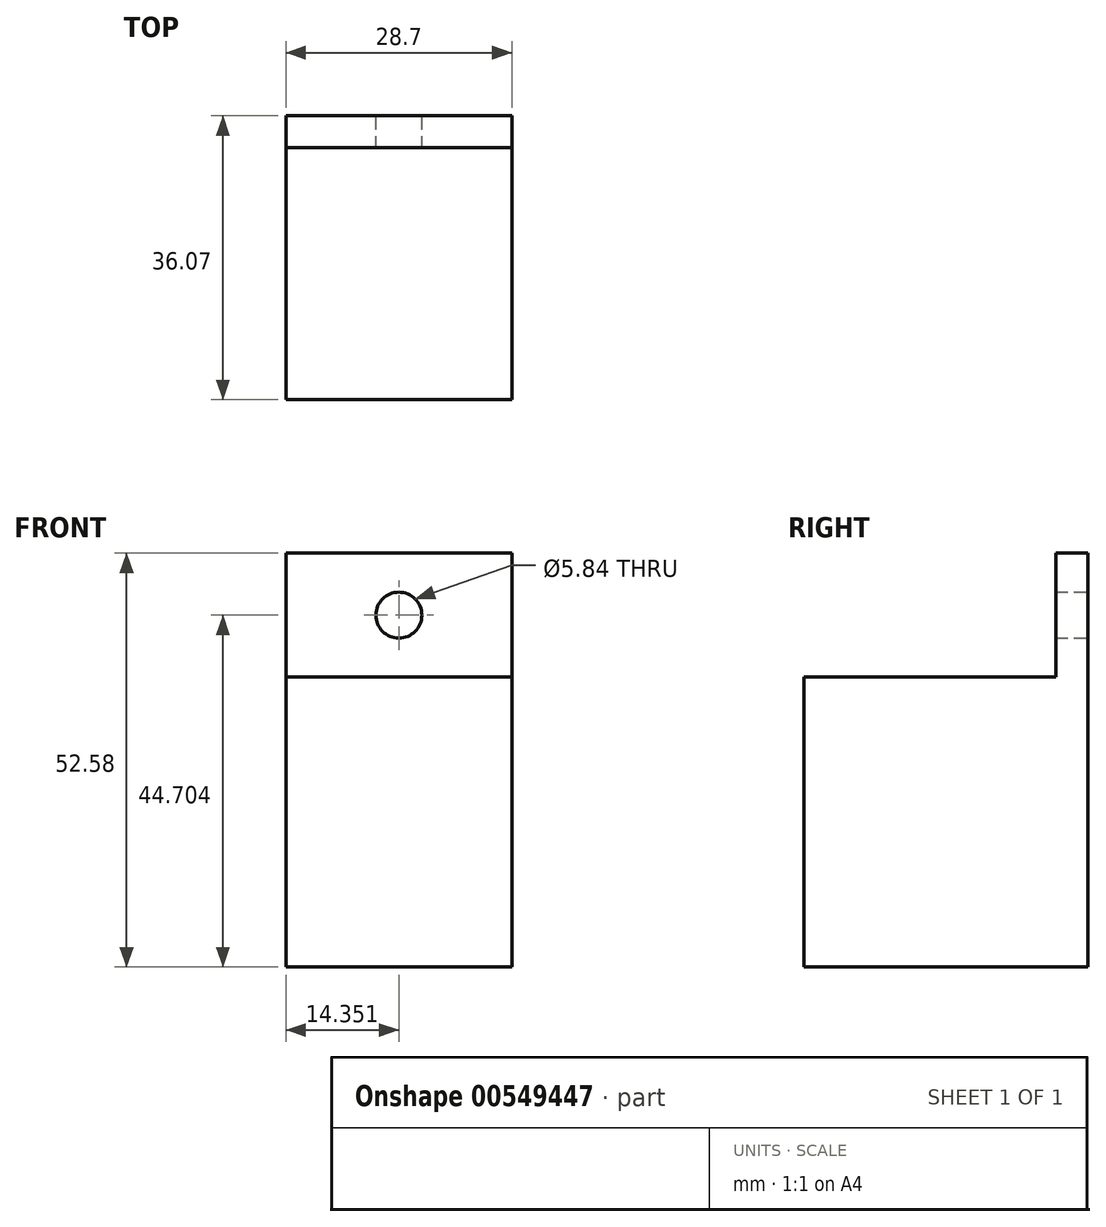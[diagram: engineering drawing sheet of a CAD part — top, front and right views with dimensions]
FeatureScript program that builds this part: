
annotation { "Feature Type Name" : "Feature", "Feature Type Description" : "" }
export const myFeature = defineFeature(function(context is Context, id is Id, definition is map)
    precondition{}
    {
        {
            var Q0;
            Q0=qCreatedBy(makeId("Right.planeOp"),FACE);
            var sketch = newSketch(context, id + "F0", { "sketchPlane" : qUnion([Q0])});
            skLineSegment(sketch, "E0", {"start": v(0, 0) * mm, "end": v(0, 52.58) * mm});
            skLineSegment(sketch, "E1", {"start": v(0, 52.58) * mm, "end": v(-4.06, 52.58) * mm});
            skLineSegment(sketch, "E2", {"start": v(-4.06, 52.58) * mm, "end": v(-4.06, 36.83) * mm});
            skLineSegment(sketch, "E3", {"start": v(-4.06, 36.83) * mm, "end": v(-36.07, 36.83) * mm});
            skLineSegment(sketch, "E4", {"start": v(-36.07, 36.83) * mm, "end": v(-36.07, 0) * mm});
            skLineSegment(sketch, "E5", {"start": v(-36.07, 0) * mm, "end": v(0, 0) * mm});
            skSolve(sketch);
        }
        {
            var Q0;
            Q0 = qSketchRegion(id + "F0", true);
            var Q1;
            Q1=makeQuery(id+"F0.imprint","IMPRINT",FACE,{"disambiguationData":[TD([[makeQuery(id+"F0.imprint","IMPRINT",EDGE,{"derivedFrom":sQuery(id+"F0.wireOp",EDGE,"E0")}),1.0]])]});
            extrude(context, id + "F1", {"entities" : qUnion([Q0, Q1]), "depth" : 28.7 * mm, "offsetDistance" : 25.4 * mm});
        }
        {
            var Q0;
            Q0=makeQuery(id+"F1.opExtrude","SWEPT_FACE",FACE,{"disambiguationData":[OSD([sQuery(id+"F0.wireOp",EDGE,"E2")])]});
            var sketch = newSketch(context, id + "F2", { "sketchPlane" : qUnion([Q0])});
            skPoint(sketch, "E6", {"position": v(14.35, 44.7) * mm});
            skPoint(sketch, "E6.positionSnap0", {"position": v(0, 44.7) * mm});
            skPoint(sketch, "E6.positionSnap1", {"position": v(14.35, 52.58) * mm});
            skSolve(sketch);
        }
        {
            var Q0;
            Q0=sQuery(id+"F2.wireOp",VERTEX,"E6");
            var Q1;
            Q1=makeQuery(id+"F1.opExtrude","SWEPT_BODY",BODY,{"disambiguationData":[OSD([sQuery(id+"F0.wireOp",EDGE,"E0"),sQuery(id+"F0.wireOp",EDGE,"E1"),sQuery(id+"F0.wireOp",EDGE,"E2"),sQuery(id+"F0.wireOp",EDGE,"E3"),sQuery(id+"F0.wireOp",EDGE,"E4"),sQuery(id+"F0.wireOp",EDGE,"E5")])]});
            hole(context, id + "F3", {"style" : HoleStyle.SIMPLE, "endStyle" : HoleEndStyle.THROUGH, "holeDiameter" : 5.84 * mm, "majorDiameter" : 6.35 * mm, "isTappedThrough" : true, "tappedDepth" : 12.7 * mm, "tapClearance" : 3, "startFromSketch" : true, "locations" : qUnion([Q0]), "scope" : qUnion([Q1])});
        }
    });
